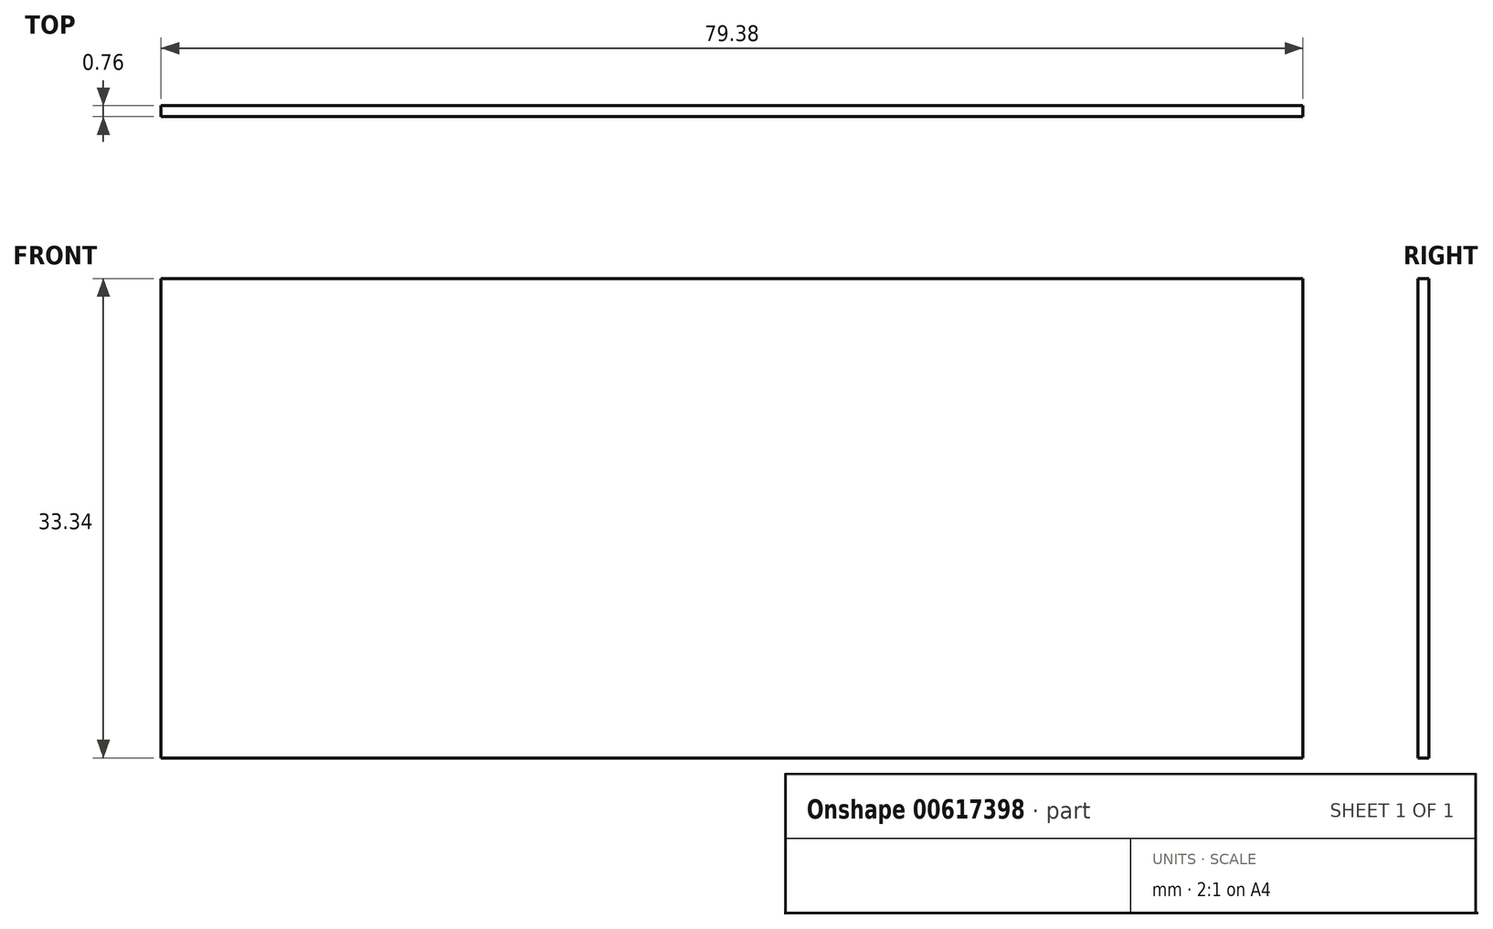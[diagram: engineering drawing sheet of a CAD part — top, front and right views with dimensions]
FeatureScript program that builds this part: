
annotation { "Feature Type Name" : "Feature", "Feature Type Description" : "" }
export const myFeature = defineFeature(function(context is Context, id is Id, definition is map)
    precondition{}
    {
        {
            var Q0;
            Q0=qCreatedBy(makeId("Front.planeOp"),FACE);
            var sketch = newSketch(context, id + "F0", { "sketchPlane" : qUnion([Q0])});
            skLineSegment(sketch, "E0.bottom", {"start": v(0, 33.34) * mm, "end": v(79.38, 33.34) * mm});
            skLineSegment(sketch, "E0.top", {"start": v(0, 0) * mm, "end": v(79.38, 0) * mm});
            skLineSegment(sketch, "E0.left", {"start": v(0, 33.34) * mm, "end": v(0, 0) * mm});
            skLineSegment(sketch, "E0.right", {"start": v(79.38, 33.34) * mm, "end": v(79.38, 0) * mm});
            skSolve(sketch);
        }
        {
            var Q0;
            Q0 = qSketchRegion(id + "F0", true);
            extrude(context, id + "F1", {"entities" : qUnion([Q0]), "depth" : 0.76 * mm, "offsetDistance" : 25.4 * mm});
        }
        {
            var Q0;
            Q0=makeQuery(id+"F1.opExtrude","SWEPT_BODY",BODY,{"disambiguationData":[OSD([sQuery(id+"F0.wireOp",EDGE,"E0.bottom"),sQuery(id+"F0.wireOp",EDGE,"E0.top"),sQuery(id+"F0.wireOp",EDGE,"E0.left"),sQuery(id+"F0.wireOp",EDGE,"E0.right")])]});
            transform(context, id + "F2", {"entities" : qUnion([Q0]), "transformType" : TransformType.TRANSLATION_3D, "dx" : 0 * mm, "dy" : 0 * mm, "dz" : -11.13 * mm, "makeCopy" : false});
        }
        {
            var Q0;
            Q0=makeQuery(id+"F1.opExtrude","SWEPT_BODY",BODY,{"disambiguationData":[OSD([sQuery(id+"F0.wireOp",EDGE,"E0.bottom"),sQuery(id+"F0.wireOp",EDGE,"E0.top"),sQuery(id+"F0.wireOp",EDGE,"E0.left"),sQuery(id+"F0.wireOp",EDGE,"E0.right")])]});
            transform(context, id + "F3", {"entities" : qUnion([Q0]), "transformType" : TransformType.TRANSLATION_3D, "dx" : 0 * mm, "dy" : 1.59 * mm, "dz" : 0 * mm, "makeCopy" : false});
        }
    });
